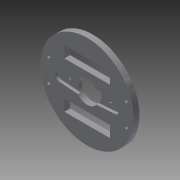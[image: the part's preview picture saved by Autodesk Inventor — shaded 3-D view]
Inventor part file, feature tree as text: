
AUTODESK INVENTOR PART (.ipt)
format: ipt  version: 2016 (Build 200138000, 138)  size: 154,112 bytes
history: native  units: mm
features: extrude x3, sketch x3, fillet x1
ambient origin geometry x8: Origin, YZ Plane, XZ Plane, XY Plane, X Axis, Y Axis, Z Axis, Center Point
bodies: Body1 (feature_tree)
feature tree (7):
  extrude  "Extrusion4"  Depth=10.0mm
  extrude  "Extrusion5"  Depth=20.0mm
  fillet  "Fillet1"  Radius=3.3mm
  extrude  "Extrusion6"  Depth=5.0mm
  sketch  "Sketch3"  dims[d4=74.558575mm d5=60.588575mm d7=10.0mm]
  sketch  "Sketch5"  dims[d8=3.0mm d9=20.0mm d11=20.0mm d12=20.0mm d14=68.0mm d17=3.3mm]
  sketch  "Sketch7"  dims[d18=18.0mm d19=2.0mm d21=5.0mm d22=10.0mm d27=5.0mm d28=0.0mm d30=13.0mm d31=28.0mm d32=4.5mm d33=4.5mm d34=2.5mm d35=0.0mm d36=4.0mm d39=20.0mm d40=5.0mm d41=0.0mm]
